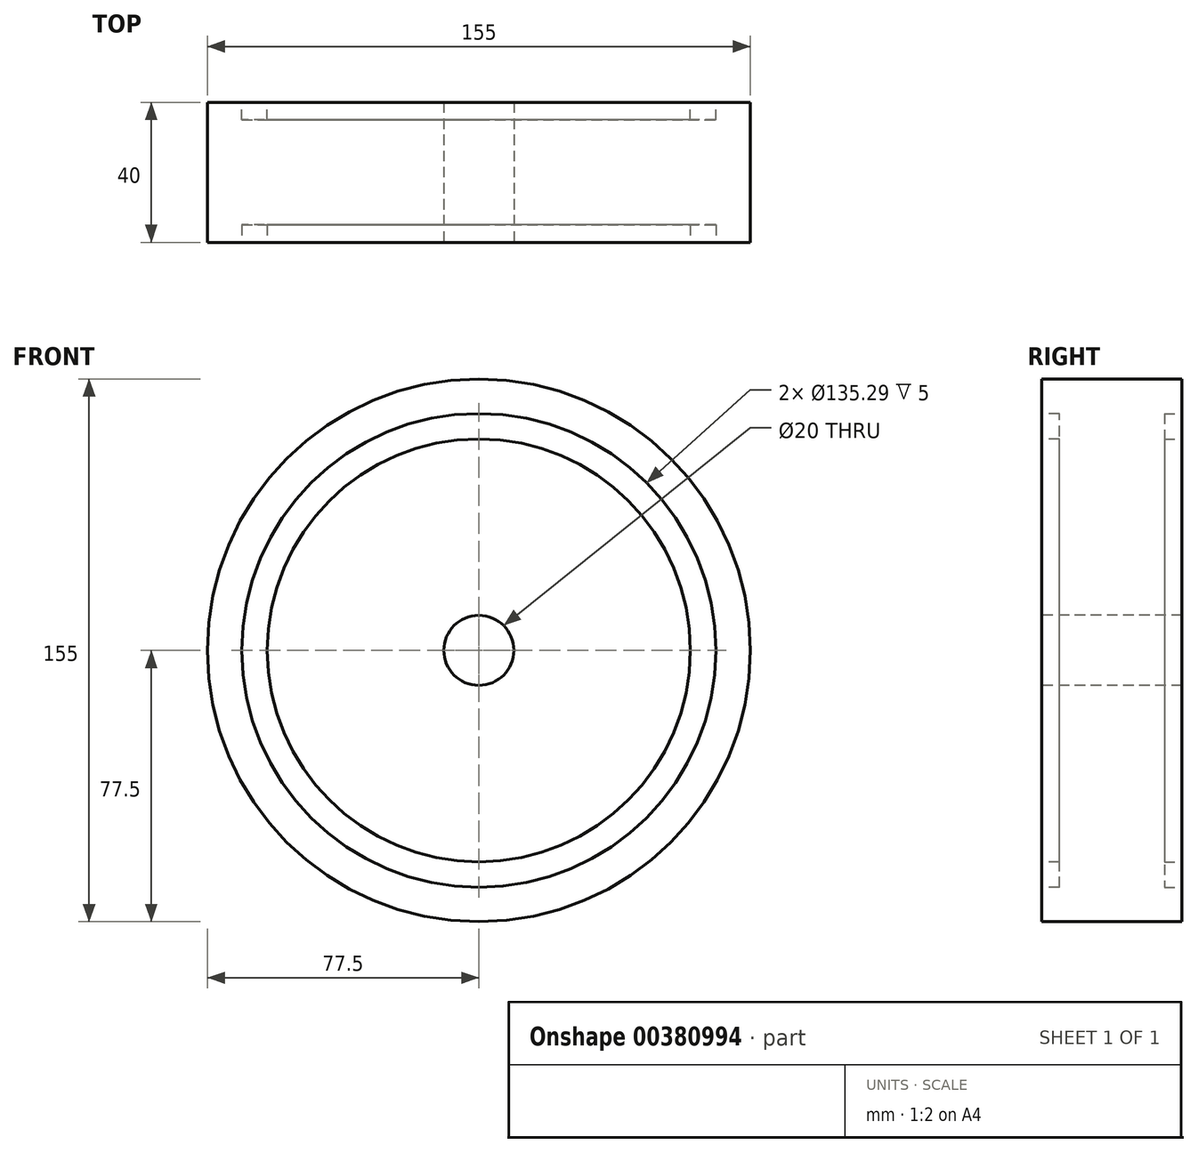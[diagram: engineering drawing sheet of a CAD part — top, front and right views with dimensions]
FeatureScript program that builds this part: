
annotation { "Feature Type Name" : "Feature", "Feature Type Description" : "" }
export const myFeature = defineFeature(function(context is Context, id is Id, definition is map)
    precondition{}
    {
        {
            var Q0;
            Q0=qCreatedBy(makeId("Front.planeOp"),FACE);
            var sketch = newSketch(context, id + "F0", { "sketchPlane" : qUnion([Q0])});
            skCircle(sketch, "E0", {"center": v(0, 0) * mm, "radius": 77.5 * mm});
            skSolve(sketch);
        }
        {
            var Q0;
            Q0=makeQuery(id+"F0.imprint","IMPRINT",FACE,{"disambiguationData":[TD([[makeQuery(id+"F0.imprint","IMPRINT",EDGE,{"derivedFrom":sQuery(id+"F0.wireOp",EDGE,"E0")}),1.0]])]});
            extrude(context, id + "F1", {"entities" : qUnion([Q0]), "endBound" : BoundingType.SYMMETRIC, "depth" : 40 * mm});
        }
        {
            var Q0;
            Q0=makeQuery(id+"F1.opExtrude","CAP_FACE",FACE,{"disambiguationData":[OSD([sQuery(id+"F0.wireOp",EDGE,"E0")])],"isStart":false});
            var sketch = newSketch(context, id + "F2", { "sketchPlane" : qUnion([Q0])});
            skCircle(sketch, "E1", {"center": v(0, 0) * mm, "radius": 67.64 * mm});
            skCircle(sketch, "E2", {"center": v(0, 0) * mm, "radius": 60.38 * mm});
            skSolve(sketch);
        }
        {
            var Q0;
            Q0=makeQuery(id+"F2.imprint","IMPRINT",FACE,{"disambiguationData":[TD([[makeQuery(id+"F2.imprint","IMPRINT",EDGE,{"derivedFrom":sQuery(id+"F2.wireOp",EDGE,"E1")}),1.0]])]});
            extrude(context, id + "F3", {"entities" : qUnion([Q0]), "operationType" : NewBodyOperationType.REMOVE, "oppositeDirection" : true, "depth" : 5 * mm});
        }
        {
            var Q0;
            Q0=makeQuery(id+"F1.opExtrude","CAP_FACE",FACE,{"disambiguationData":[OSD([sQuery(id+"F0.wireOp",EDGE,"E0")])],"isStart":true});
            var sketch = newSketch(context, id + "F4", { "sketchPlane" : qUnion([Q0])});
            skCircle(sketch, "E3", {"center": v(0, 0) * mm, "radius": 67.64 * mm});
            skCircle(sketch, "E4", {"center": v(0, 0) * mm, "radius": 60.38 * mm});
            skSolve(sketch);
        }
        {
            var Q0;
            Q0 = qSketchRegion(id + "F4", true);
            extrude(context, id + "F5", {"entities" : qUnion([Q0]), "operationType" : NewBodyOperationType.REMOVE, "oppositeDirection" : true, "depth" : 5 * mm});
        }
        {
            var Q0;
            Q0=makeQuery(id+"F3.boolean.opBoolean","SPLIT",FACE,{"disambiguationData":[TD([makeQuery(id+"F3.opExtrude","SWEPT_FACE",FACE,{"disambiguationData":[OSD([sQuery(id+"F2.wireOp",EDGE,"E2")])]})])],"derivedFrom":makeQuery(id+"F1.opExtrude","CAP_FACE",FACE,{"disambiguationData":[OSD([sQuery(id+"F0.wireOp",EDGE,"E0")])],"isStart":false})});
            var sketch = newSketch(context, id + "F6", { "sketchPlane" : qUnion([Q0])});
            skCircle(sketch, "E5", {"center": v(0, 0) * mm, "radius": 10 * mm});
            skSolve(sketch);
        }
        {
            var Q0;
            Q0=makeQuery(id+"F6.imprint","IMPRINT",FACE,{"disambiguationData":[TD([[makeQuery(id+"F6.imprint","IMPRINT",EDGE,{"derivedFrom":sQuery(id+"F6.wireOp",EDGE,"E5")}),1.0]])]});
            extrude(context, id + "F7", {"entities" : qUnion([Q0]), "operationType" : NewBodyOperationType.REMOVE, "endBound" : BoundingType.THROUGH_ALL, "oppositeDirection" : true, "depth" : 25 * mm});
        }
    });
